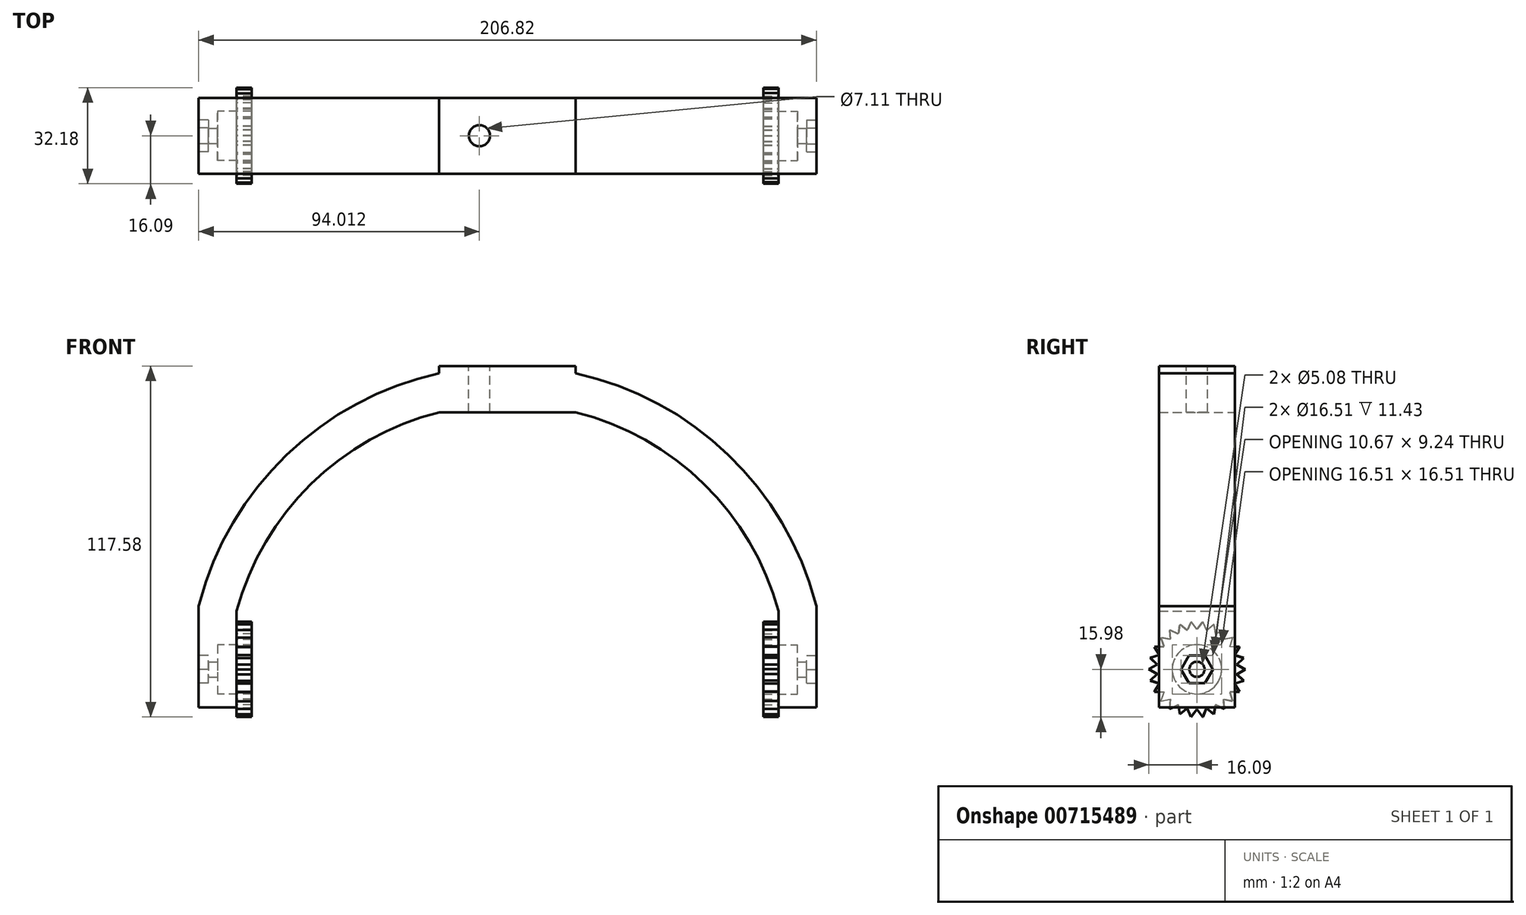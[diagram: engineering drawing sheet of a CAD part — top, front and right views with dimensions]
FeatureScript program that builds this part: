
annotation { "Feature Type Name" : "Feature", "Feature Type Description" : "" }
export const myFeature = defineFeature(function(context is Context, id is Id, definition is map)
    precondition{}
    {
        {
            var Q0;
            Q0=qCreatedBy(makeId("Front.planeOp"),FACE);
            var sketch = newSketch(context, id + "F0", { "sketchPlane" : qUnion([Q0])});
            skArc(sketch, "E0", {"start": v(97.06, 33.02) * mm, "mid": v(0, 107.95) * mm, "end": v(-97.06, 33.02) * mm});
            skLineSegment(sketch, "E1", {"start": v(-97.06, 33.02) * mm, "end": v(-97.06, 0) * mm});
            skLineSegment(sketch, "E2", {"start": v(97.06, 33.02) * mm, "end": v(97.06, 0) * mm});
            skSolve(sketch);
        }
        {
            var Q0;
            Q0=qCreatedBy(makeId("Top.planeOp"),FACE);
            var sketch = newSketch(context, id + "F1", { "sketchPlane" : qUnion([Q0])});
            skPoint(sketch, "E3.0", {"position": v(-97.06, 0) * mm});
            skLineSegment(sketch, "E4.bottom", {"start": v(-103.41, 12.7) * mm, "end": v(-90.71, 12.7) * mm});
            skLineSegment(sketch, "E4.top", {"start": v(-103.41, -12.7) * mm, "end": v(-90.71, -12.7) * mm});
            skLineSegment(sketch, "E4.left", {"start": v(-103.41, 12.7) * mm, "end": v(-103.41, -12.7) * mm});
            skLineSegment(sketch, "E4.right", {"start": v(-90.71, 12.7) * mm, "end": v(-90.71, -12.7) * mm});
            skSolve(sketch);
        }
        {
            var Q0;
            Q0=qSketchRegion(id+"F1",true);
            var Q1;
            Q1=qConstructionFilter(qBodyType(qCreatedBy(id+"F0",EDGE),BodyType.WIRE),ConstructionObject.NO);
            sweep(context, id + "F2", {"profiles" : qUnion([Q0]), "path" : qUnion([Q1])});
        }
        {
            var Q0;
            Q0=qCreatedBy(makeId("Right.planeOp"),FACE);
            var sketch = newSketch(context, id + "F3", { "sketchPlane" : qUnion([Q0])});
            skCircle(sketch, "E5", {"center": v(0, 12.7) * mm, "radius": 2.54 * mm});
            skSolve(sketch);
        }
        {
            var Q0;
            Q0=qSketchRegion(id+"F3",true);
            extrude(context, id + "F4", {"entities" : qUnion([Q0]), "operationType" : NewBodyOperationType.REMOVE, "endBound" : BoundingType.SYMMETRIC, "oppositeDirection" : true, "depth" : 254 * mm, "offsetDistance" : 25.4 * mm});
        }
        {
            var Q0;
            Q0=makeQuery(id+"F2.opSweep","SWEPT_FACE",FACE,{"disambiguationData":[OSD([sQuery(id+"F0.wireOp",EDGE,"E2"),sQuery(id+"F1.wireOp",EDGE,"E4.left")])]});
            var Q1;
            Q1=makeQuery(id+"F2.opSweep","CAP_VERTEX",VERTEX,{"disambiguationData":[OSD([sQuery(id+"F0.wireOp",EDGE,"E2"),sQuery(id+"F1.wireOp",EDGE,"E4.bottom"),sQuery(id+"F1.wireOp",EDGE,"E4.left")])],"isStart":false});
            cPlane(context, id + "F5", {"entities" : qUnion([Q0, Q1]), "cplaneType" : CPlaneType.PLANE_POINT, "offset" : 25.4 * mm, "width" : 152.4 * mm, "height" : 152.4 * mm});
        }
        {
            var Q0;
            Q0=qCreatedBy(id+"F5.planeOp",FACE);
            var sketch = newSketch(context, id + "F6", { "sketchPlane" : qUnion([Q0])});
            skCircle(sketch, "E6", {"center": v(0, 12.7) * mm, "radius": 5.33 * mm, "construction": true});
            skLineSegment(sketch, "E7.0", {"start": v(-2.67, 17.32) * mm, "end": v(2.67, 17.32) * mm});
            skLineSegment(sketch, "E7.1", {"start": v(2.67, 17.32) * mm, "end": v(5.33, 12.7) * mm});
            skLineSegment(sketch, "E7.2", {"start": v(5.33, 12.7) * mm, "end": v(2.67, 8.08) * mm});
            skLineSegment(sketch, "E7.3", {"start": v(2.67, 8.08) * mm, "end": v(-2.67, 8.08) * mm});
            skLineSegment(sketch, "E7.4", {"start": v(-2.67, 8.08) * mm, "end": v(-5.33, 12.7) * mm});
            skLineSegment(sketch, "E7.5", {"start": v(-5.33, 12.7) * mm, "end": v(-2.67, 17.32) * mm});
            skSolve(sketch);
        }
        {
            var Q0;
            Q0=makeQuery(id+"F6.imprint","IMPRINT",FACE,{"disambiguationData":[TD([[makeQuery(id+"F6.imprint","IMPRINT",EDGE,{"derivedFrom":sQuery(id+"F6.wireOp",EDGE,"E7.0")}),-1.0]])]});
            extrude(context, id + "F7", {"entities" : qUnion([Q0]), "operationType" : NewBodyOperationType.REMOVE, "oppositeDirection" : true, "depth" : 3.3 * mm, "offsetDistance" : 25.4 * mm});
        }
        {
            var Q0;
            Q0=makeQuery(id+"F2.opSweep","SWEPT_FACE",FACE,{"disambiguationData":[OSD([sQuery(id+"F0.wireOp",EDGE,"E1"),sQuery(id+"F1.wireOp",EDGE,"E4.left")])]});
            var Q1;
            Q1=makeQuery(id+"F2.opSweep","CAP_VERTEX",VERTEX,{"disambiguationData":[OSD([sQuery(id+"F0.wireOp",EDGE,"E1"),sQuery(id+"F1.wireOp",EDGE,"E4.bottom"),sQuery(id+"F1.wireOp",EDGE,"E4.left")])],"isStart":true});
            cPlane(context, id + "F8", {"entities" : qUnion([Q0, Q1]), "cplaneType" : CPlaneType.PLANE_POINT, "offset" : 25.4 * mm, "width" : 152.4 * mm, "height" : 152.4 * mm});
        }
        {
            var Q0;
            Q0=qCreatedBy(id+"F8.planeOp",FACE);
            var sketch = newSketch(context, id + "F9", { "sketchPlane" : qUnion([Q0])});
            skLineSegment(sketch, "E8", {"start": v(0, 0) * mm, "end": v(0, 12.7) * mm, "construction": true});
            skCircle(sketch, "E9", {"center": v(0, 12.7) * mm, "radius": 5.33 * mm, "construction": true});
            skLineSegment(sketch, "E10.0", {"start": v(-2.67, 17.32) * mm, "end": v(2.67, 17.32) * mm});
            skLineSegment(sketch, "E10.1", {"start": v(2.67, 17.32) * mm, "end": v(5.33, 12.7) * mm});
            skLineSegment(sketch, "E10.2", {"start": v(5.33, 12.7) * mm, "end": v(2.67, 8.08) * mm});
            skLineSegment(sketch, "E10.3", {"start": v(2.67, 8.08) * mm, "end": v(-2.67, 8.08) * mm});
            skLineSegment(sketch, "E10.4", {"start": v(-2.67, 8.08) * mm, "end": v(-5.33, 12.7) * mm});
            skLineSegment(sketch, "E10.5", {"start": v(-5.33, 12.7) * mm, "end": v(-2.67, 17.32) * mm});
            skSolve(sketch);
        }
        {
            var Q0;
            Q0=makeQuery(id+"F9.imprint","IMPRINT",FACE,{"disambiguationData":[TD([[makeQuery(id+"F9.imprint","IMPRINT",EDGE,{"derivedFrom":sQuery(id+"F9.wireOp",EDGE,"E10.0")}),-1.0]])]});
            extrude(context, id + "F10", {"entities" : qUnion([Q0]), "operationType" : NewBodyOperationType.REMOVE, "oppositeDirection" : true, "depth" : 3.3 * mm, "offsetDistance" : 25.4 * mm});
        }
        {
            var Q0;
            Q0=makeQuery(id+"F2.opSweep","SWEPT_FACE",FACE,{"disambiguationData":[OSD([sQuery(id+"F0.wireOp",EDGE,"E1"),sQuery(id+"F1.wireOp",EDGE,"E4.left")])]});
            cPlane(context, id + "F11", {"entities" : qUnion([Q0]), "cplaneType" : CPlaneType.OFFSET, "offset" : 6.35 * mm, "oppositeDirection" : true, "width" : 152.4 * mm, "height" : 152.4 * mm});
        }
        {
            var Q0;
            Q0=qCreatedBy(id+"F11.planeOp",FACE);
            var sketch = newSketch(context, id + "F12", { "sketchPlane" : qUnion([Q0])});
            skLineSegment(sketch, "E11", {"start": v(0, 0) * mm, "end": v(0, 12.7) * mm, "construction": true});
            skCircle(sketch, "E12", {"center": v(0, 12.7) * mm, "radius": 8.26 * mm});
            skSolve(sketch);
        }
        {
            var Q0;
            Q0=makeQuery(id+"F2.opSweep","SWEPT_FACE",FACE,{"disambiguationData":[OSD([sQuery(id+"F0.wireOp",EDGE,"E2"),sQuery(id+"F1.wireOp",EDGE,"E4.left")])]});
            cPlane(context, id + "F13", {"entities" : qUnion([Q0]), "cplaneType" : CPlaneType.OFFSET, "offset" : 6.35 * mm, "oppositeDirection" : true, "width" : 152.4 * mm, "height" : 152.4 * mm});
        }
        {
            var Q0;
            Q0=qCreatedBy(id+"F13.planeOp",FACE);
            var sketch = newSketch(context, id + "F14", { "sketchPlane" : qUnion([Q0])});
            skLineSegment(sketch, "E13", {"start": v(0, 0) * mm, "end": v(0, 12.7) * mm, "construction": true});
            skCircle(sketch, "E14", {"center": v(0, 12.7) * mm, "radius": 8.26 * mm});
            skSolve(sketch);
        }
        {
            var Q0;
            Q0=makeQuery(id+"F2.opSweep","SWEPT_FACE",FACE,{"disambiguationData":[OSD([sQuery(id+"F0.wireOp",EDGE,"E1"),sQuery(id+"F1.wireOp",EDGE,"E4.right")])]});
            var sketch = newSketch(context, id + "F15", { "sketchPlane" : qUnion([Q0])});
            skCircle(sketch, "E15", {"center": v(0, 12.7) * mm, "radius": 13.34 * mm, "construction": true});
            skLineSegment(sketch, "E16", {"start": v(-3.28, 25.63) * mm, "end": v(-2, 28.67) * mm});
            skLineSegment(sketch, "E17", {"start": v(-2, 28.67) * mm, "end": v(0, 26.04) * mm});
            skLineSegment(sketch, "E18.1.0", {"start": v(-6.27, 24.47) * mm, "end": v(-5.76, 27.73) * mm});
            skLineSegment(sketch, "E18.1.1", {"start": v(-5.76, 27.73) * mm, "end": v(-3.2, 25.65) * mm});
            skLineSegment(sketch, "E18.2.0", {"start": v(-8.9, 22.62) * mm, "end": v(-9.18, 25.91) * mm});
            skLineSegment(sketch, "E18.2.1", {"start": v(-9.18, 25.91) * mm, "end": v(-6.2, 24.5) * mm});
            skLineSegment(sketch, "E18.3.0", {"start": v(-11.02, 20.2) * mm, "end": v(-12.08, 23.33) * mm});
            skLineSegment(sketch, "E18.3.1", {"start": v(-12.08, 23.33) * mm, "end": v(-8.84, 22.68) * mm});
            skLineSegment(sketch, "E18.4.0", {"start": v(-12.5, 17.35) * mm, "end": v(-14.27, 20.13) * mm});
            skLineSegment(sketch, "E18.4.1", {"start": v(-14.27, 20.13) * mm, "end": v(-10.97, 20.28) * mm});
            skLineSegment(sketch, "E18.5.0", {"start": v(-13.25, 14.22) * mm, "end": v(-15.64, 16.5) * mm});
            skLineSegment(sketch, "E18.5.1", {"start": v(-15.64, 16.5) * mm, "end": v(-12.47, 17.43) * mm});
            skLineSegment(sketch, "E18.6.0", {"start": v(-13.23, 11) * mm, "end": v(-16.1, 12.65) * mm});
            skLineSegment(sketch, "E18.6.1", {"start": v(-16.1, 12.65) * mm, "end": v(-13.24, 14.3) * mm});
            skLineSegment(sketch, "E18.7.0", {"start": v(-12.44, 7.89) * mm, "end": v(-15.61, 8.8) * mm});
            skLineSegment(sketch, "E18.7.1", {"start": v(-15.61, 8.8) * mm, "end": v(-13.24, 11.1) * mm});
            skLineSegment(sketch, "E18.8.0", {"start": v(-10.92, 5.05) * mm, "end": v(-14.22, 5.17) * mm});
            skLineSegment(sketch, "E18.8.1", {"start": v(-14.22, 5.17) * mm, "end": v(-12.47, 7.97) * mm});
            skLineSegment(sketch, "E18.9.0", {"start": v(-8.78, 2.66) * mm, "end": v(-12, 1.99) * mm});
            skLineSegment(sketch, "E18.9.1", {"start": v(-12, 1.99) * mm, "end": v(-10.97, 5.12) * mm});
            skLineSegment(sketch, "E18.10.0", {"start": v(-6.12, 0.85) * mm, "end": v(-9.1, -0.57) * mm});
            skLineSegment(sketch, "E18.10.1", {"start": v(-9.1, -0.57) * mm, "end": v(-8.84, 2.72) * mm});
            skLineSegment(sketch, "E18.11.0", {"start": v(-3.1, -0.27) * mm, "end": v(-5.66, -2.37) * mm});
            skLineSegment(sketch, "E18.11.1", {"start": v(-5.66, -2.37) * mm, "end": v(-6.2, 0.9) * mm});
            skLineSegment(sketch, "E18.12.0", {"start": v(0.09, -0.63) * mm, "end": v(-1.89, -3.28) * mm});
            skLineSegment(sketch, "E18.12.1", {"start": v(-1.89, -3.28) * mm, "end": v(-3.2, -0.25) * mm});
            skLineSegment(sketch, "E18.13.0", {"start": v(3.28, -0.23) * mm, "end": v(2, -3.27) * mm});
            skLineSegment(sketch, "E18.13.1", {"start": v(2, -3.27) * mm, "end": v(0, -0.63) * mm});
            skLineSegment(sketch, "E18.14.0", {"start": v(6.27, 0.93) * mm, "end": v(5.76, -2.33) * mm});
            skLineSegment(sketch, "E18.14.1", {"start": v(5.76, -2.33) * mm, "end": v(3.2, -0.25) * mm});
            skLineSegment(sketch, "E18.15.0", {"start": v(8.9, 2.78) * mm, "end": v(9.18, -0.51) * mm});
            skLineSegment(sketch, "E18.15.1", {"start": v(9.18, -0.51) * mm, "end": v(6.2, 0.9) * mm});
            skLineSegment(sketch, "E18.16.0", {"start": v(11.02, 5.2) * mm, "end": v(12.08, 2.07) * mm});
            skLineSegment(sketch, "E18.16.1", {"start": v(12.08, 2.07) * mm, "end": v(8.84, 2.72) * mm});
            skLineSegment(sketch, "E18.17.0", {"start": v(12.5, 8.05) * mm, "end": v(14.27, 5.27) * mm});
            skLineSegment(sketch, "E18.17.1", {"start": v(14.27, 5.27) * mm, "end": v(10.97, 5.12) * mm});
            skLineSegment(sketch, "E18.18.0", {"start": v(13.25, 11.18) * mm, "end": v(15.64, 8.9) * mm});
            skLineSegment(sketch, "E18.18.1", {"start": v(15.64, 8.9) * mm, "end": v(12.47, 7.97) * mm});
            skLineSegment(sketch, "E18.19.0", {"start": v(13.23, 14.4) * mm, "end": v(16.1, 12.75) * mm});
            skLineSegment(sketch, "E18.19.1", {"start": v(16.1, 12.75) * mm, "end": v(13.24, 11.1) * mm});
            skLineSegment(sketch, "E18.20.0", {"start": v(12.44, 17.51) * mm, "end": v(15.61, 16.6) * mm});
            skLineSegment(sketch, "E18.20.1", {"start": v(15.61, 16.6) * mm, "end": v(13.24, 14.3) * mm});
            skLineSegment(sketch, "E18.21.0", {"start": v(10.92, 20.35) * mm, "end": v(14.22, 20.23) * mm});
            skLineSegment(sketch, "E18.21.1", {"start": v(14.22, 20.23) * mm, "end": v(12.47, 17.43) * mm});
            skLineSegment(sketch, "E18.22.0", {"start": v(8.78, 22.74) * mm, "end": v(12, 23.41) * mm});
            skLineSegment(sketch, "E18.22.1", {"start": v(12, 23.41) * mm, "end": v(10.97, 20.28) * mm});
            skLineSegment(sketch, "E18.23.0", {"start": v(6.12, 24.55) * mm, "end": v(9.1, 25.97) * mm});
            skLineSegment(sketch, "E18.23.1", {"start": v(9.1, 25.97) * mm, "end": v(8.84, 22.68) * mm});
            skLineSegment(sketch, "E18.24.0", {"start": v(3.1, 25.67) * mm, "end": v(5.66, 27.77) * mm});
            skLineSegment(sketch, "E18.24.1", {"start": v(5.66, 27.77) * mm, "end": v(6.2, 24.5) * mm});
            skLineSegment(sketch, "E18.25.0", {"start": v(-0.09, 26.03) * mm, "end": v(1.89, 28.68) * mm});
            skLineSegment(sketch, "E18.25.1", {"start": v(1.89, 28.68) * mm, "end": v(3.2, 25.65) * mm});
            skSolve(sketch);
        }
        {
            var Q0;
            Q0=qSketchRegion(id+"F15",true);
            extrude(context, id + "F16", {"entities" : qUnion([Q0]), "operationType" : NewBodyOperationType.ADD, "depth" : 5.08 * mm, "offsetDistance" : 25.4 * mm});
        }
        {
            var Q0;
            Q0=makeQuery(id+"F2.opSweep","SWEPT_FACE",FACE,{"disambiguationData":[OSD([sQuery(id+"F0.wireOp",EDGE,"E2"),sQuery(id+"F1.wireOp",EDGE,"E4.right")])]});
            var sketch = newSketch(context, id + "F17", { "sketchPlane" : qUnion([Q0])});
            skCircle(sketch, "E19", {"center": v(0, 12.7) * mm, "radius": 13.34 * mm, "construction": true});
            skLineSegment(sketch, "E20", {"start": v(-3.28, 25.63) * mm, "end": v(-2, 28.67) * mm});
            skLineSegment(sketch, "E21", {"start": v(-2, 28.67) * mm, "end": v(0, 26.04) * mm});
            skLineSegment(sketch, "E22.1.0", {"start": v(-5.76, 27.73) * mm, "end": v(-3.2, 25.65) * mm});
            skLineSegment(sketch, "E22.1.1", {"start": v(-6.27, 24.47) * mm, "end": v(-5.76, 27.73) * mm});
            skLineSegment(sketch, "E22.2.0", {"start": v(-9.18, 25.91) * mm, "end": v(-6.2, 24.5) * mm});
            skLineSegment(sketch, "E22.2.1", {"start": v(-8.9, 22.62) * mm, "end": v(-9.18, 25.91) * mm});
            skLineSegment(sketch, "E22.3.0", {"start": v(-12.08, 23.33) * mm, "end": v(-8.84, 22.68) * mm});
            skLineSegment(sketch, "E22.3.1", {"start": v(-11.02, 20.2) * mm, "end": v(-12.08, 23.33) * mm});
            skLineSegment(sketch, "E22.4.0", {"start": v(-14.27, 20.13) * mm, "end": v(-10.97, 20.28) * mm});
            skLineSegment(sketch, "E22.4.1", {"start": v(-12.5, 17.35) * mm, "end": v(-14.27, 20.13) * mm});
            skLineSegment(sketch, "E22.5.0", {"start": v(-15.64, 16.5) * mm, "end": v(-12.47, 17.43) * mm});
            skLineSegment(sketch, "E22.5.1", {"start": v(-13.25, 14.22) * mm, "end": v(-15.64, 16.5) * mm});
            skLineSegment(sketch, "E22.6.0", {"start": v(-16.1, 12.65) * mm, "end": v(-13.24, 14.3) * mm});
            skLineSegment(sketch, "E22.6.1", {"start": v(-13.23, 11) * mm, "end": v(-16.1, 12.65) * mm});
            skLineSegment(sketch, "E22.7.0", {"start": v(-15.61, 8.8) * mm, "end": v(-13.24, 11.1) * mm});
            skLineSegment(sketch, "E22.7.1", {"start": v(-12.44, 7.89) * mm, "end": v(-15.61, 8.8) * mm});
            skLineSegment(sketch, "E22.8.0", {"start": v(-14.22, 5.17) * mm, "end": v(-12.47, 7.97) * mm});
            skLineSegment(sketch, "E22.8.1", {"start": v(-10.92, 5.05) * mm, "end": v(-14.22, 5.17) * mm});
            skLineSegment(sketch, "E22.9.0", {"start": v(-12, 1.99) * mm, "end": v(-10.97, 5.12) * mm});
            skLineSegment(sketch, "E22.9.1", {"start": v(-8.78, 2.66) * mm, "end": v(-12, 1.99) * mm});
            skLineSegment(sketch, "E22.10.0", {"start": v(-9.1, -0.57) * mm, "end": v(-8.84, 2.72) * mm});
            skLineSegment(sketch, "E22.10.1", {"start": v(-6.12, 0.85) * mm, "end": v(-9.1, -0.57) * mm});
            skLineSegment(sketch, "E22.11.0", {"start": v(-5.66, -2.37) * mm, "end": v(-6.2, 0.9) * mm});
            skLineSegment(sketch, "E22.11.1", {"start": v(-3.1, -0.27) * mm, "end": v(-5.66, -2.37) * mm});
            skLineSegment(sketch, "E22.12.0", {"start": v(-1.89, -3.28) * mm, "end": v(-3.2, -0.25) * mm});
            skLineSegment(sketch, "E22.12.1", {"start": v(0.09, -0.63) * mm, "end": v(-1.89, -3.28) * mm});
            skLineSegment(sketch, "E22.13.0", {"start": v(2, -3.27) * mm, "end": v(0, -0.63) * mm});
            skLineSegment(sketch, "E22.13.1", {"start": v(3.28, -0.23) * mm, "end": v(2, -3.27) * mm});
            skLineSegment(sketch, "E22.14.0", {"start": v(5.76, -2.33) * mm, "end": v(3.2, -0.25) * mm});
            skLineSegment(sketch, "E22.14.1", {"start": v(6.27, 0.93) * mm, "end": v(5.76, -2.33) * mm});
            skLineSegment(sketch, "E22.15.0", {"start": v(9.18, -0.51) * mm, "end": v(6.2, 0.9) * mm});
            skLineSegment(sketch, "E22.15.1", {"start": v(8.9, 2.78) * mm, "end": v(9.18, -0.51) * mm});
            skLineSegment(sketch, "E22.16.0", {"start": v(12.08, 2.07) * mm, "end": v(8.84, 2.72) * mm});
            skLineSegment(sketch, "E22.16.1", {"start": v(11.02, 5.2) * mm, "end": v(12.08, 2.07) * mm});
            skLineSegment(sketch, "E22.17.0", {"start": v(14.27, 5.27) * mm, "end": v(10.97, 5.12) * mm});
            skLineSegment(sketch, "E22.17.1", {"start": v(12.5, 8.05) * mm, "end": v(14.27, 5.27) * mm});
            skLineSegment(sketch, "E22.18.0", {"start": v(15.64, 8.9) * mm, "end": v(12.47, 7.97) * mm});
            skLineSegment(sketch, "E22.18.1", {"start": v(13.25, 11.18) * mm, "end": v(15.64, 8.9) * mm});
            skLineSegment(sketch, "E22.19.0", {"start": v(16.1, 12.75) * mm, "end": v(13.24, 11.1) * mm});
            skLineSegment(sketch, "E22.19.1", {"start": v(13.23, 14.4) * mm, "end": v(16.1, 12.75) * mm});
            skLineSegment(sketch, "E22.20.0", {"start": v(15.61, 16.6) * mm, "end": v(13.24, 14.3) * mm});
            skLineSegment(sketch, "E22.20.1", {"start": v(12.44, 17.51) * mm, "end": v(15.61, 16.6) * mm});
            skLineSegment(sketch, "E22.21.0", {"start": v(14.22, 20.23) * mm, "end": v(12.47, 17.43) * mm});
            skLineSegment(sketch, "E22.21.1", {"start": v(10.92, 20.35) * mm, "end": v(14.22, 20.23) * mm});
            skLineSegment(sketch, "E22.22.0", {"start": v(12, 23.41) * mm, "end": v(10.97, 20.28) * mm});
            skLineSegment(sketch, "E22.22.1", {"start": v(8.78, 22.74) * mm, "end": v(12, 23.41) * mm});
            skLineSegment(sketch, "E22.23.0", {"start": v(9.1, 25.97) * mm, "end": v(8.84, 22.68) * mm});
            skLineSegment(sketch, "E22.23.1", {"start": v(6.12, 24.55) * mm, "end": v(9.1, 25.97) * mm});
            skLineSegment(sketch, "E22.24.0", {"start": v(5.66, 27.77) * mm, "end": v(6.2, 24.5) * mm});
            skLineSegment(sketch, "E22.24.1", {"start": v(3.1, 25.67) * mm, "end": v(5.66, 27.77) * mm});
            skLineSegment(sketch, "E22.25.0", {"start": v(1.89, 28.68) * mm, "end": v(3.2, 25.65) * mm});
            skLineSegment(sketch, "E22.25.1", {"start": v(-0.09, 26.03) * mm, "end": v(1.89, 28.68) * mm});
            skSolve(sketch);
        }
        {
            var Q0;
            Q0=qSketchRegion(id+"F17",true);
            var Q1;
            Q1=makeQuery(id+"F2.opSweep","SWEPT_FACE",FACE,{"disambiguationData":[OSD([sQuery(id+"F0.wireOp",EDGE,"E2"),sQuery(id+"F1.wireOp",EDGE,"E4.left")])]});
            extrude(context, id + "F18", {"entities" : qUnion([Q0, Q1]), "operationType" : NewBodyOperationType.ADD, "depth" : 5.08 * mm, "offsetDistance" : 25.4 * mm});
        }
        {
            var Q0;
            Q0=qSketchRegion(id+"F12",true);
            extrude(context, id + "F19", {"entities" : qUnion([Q0]), "operationType" : NewBodyOperationType.REMOVE, "oppositeDirection" : true, "depth" : 63.75 * mm, "offsetDistance" : 25.4 * mm});
        }
        {
            var Q0;
            Q0=qSketchRegion(id+"F14",true);
            extrude(context, id + "F20", {"entities" : qUnion([Q0]), "operationType" : NewBodyOperationType.REMOVE, "oppositeDirection" : true, "depth" : 25.4 * mm, "offsetDistance" : 25.4 * mm});
        }
        {
            var Q0;
            Q0=makeQuery(id+"F2.opSweep","SWEPT_EDGE",EDGE,{"disambiguationData":[OSD([sQuery(id+"F0.wireOp",EDGE,"E0"),sQuery(id+"F1.wireOp",EDGE,"E4.top"),sQuery(id+"F1.wireOp",EDGE,"E4.left")]),OD(2.0)]});
            cPoint(context, id + "F21", {"entities" : qUnion([Q0]), "parameter" : 0.5});
        }
        {
            var Q0;
            Q0=qCreatedBy(makeId("Top.planeOp"),FACE);
            var Q1;
            Q1=qCreatedBy(id+"F21",VERTEX);
            cPlane(context, id + "F22", {"entities" : qUnion([Q0, Q1]), "cplaneType" : CPlaneType.PLANE_POINT, "offset" : 25.4 * mm, "width" : 152.4 * mm, "height" : 152.4 * mm});
        }
        {
            var Q0;
            Q0=qCreatedBy(id+"F22.planeOp",FACE);
            var sketch = newSketch(context, id + "F23", { "sketchPlane" : qUnion([Q0])});
            skFitSpline(sketch, "E23.0", {"points": [v(-103.2, 12.7) * mm, v(-34.4, 12.7) * mm, v(34.4, 12.7) * mm, v(103.2, 12.7) * mm]});
            skLineSegment(sketch, "E24.bottom", {"start": v(-22.86, 12.7) * mm, "end": v(22.86, 12.7) * mm});
            skLineSegment(sketch, "E24.top", {"start": v(-22.86, -12.7) * mm, "end": v(22.86, -12.7) * mm});
            skLineSegment(sketch, "E24.left", {"start": v(-22.86, 12.7) * mm, "end": v(-22.86, -12.7) * mm});
            skLineSegment(sketch, "E24.right", {"start": v(22.86, 12.7) * mm, "end": v(22.86, -12.7) * mm});
            skPoint(sketch, "E24.middle", {"position": v(0, 0) * mm});
            skSolve(sketch);
        }
        {
            var Q0;
            Q0=qSketchRegion(id+"F23",true);
            extrude(context, id + "F24", {"entities" : qUnion([Q0]), "operationType" : NewBodyOperationType.ADD, "oppositeDirection" : true, "depth" : 15.5 * mm, "offsetDistance" : 25.4 * mm});
        }
        {
            var Q0;
            Q0=qCreatedBy(id+"F22.planeOp",FACE);
            var sketch = newSketch(context, id + "F25", { "sketchPlane" : qUnion([Q0])});
            skCircle(sketch, "E25", {"center": v(-9.4, 0) * mm, "radius": 3.56 * mm});
            skCircle(sketch, "E26.MirrorC", {"center": v(9.4, 0) * mm, "radius": 3.56 * mm});
            skSolve(sketch);
        }
        {
            var Q0;
            Q0=makeQuery(id+"F25.imprint","IMPRINT",FACE,{"disambiguationData":[TD([[makeQuery(id+"F25.imprint","IMPRINT",EDGE,{"derivedFrom":sQuery(id+"F25.wireOp",EDGE,"E25")}),1.0]])]});
            var Q1;
            Q1=makeQuery(id+"F25.imprint","IMPRINT",FACE,{"disambiguationData":[TD([[makeQuery(id+"F25.imprint","IMPRINT",EDGE,{"derivedFrom":sQuery(id+"F25.wireOp",EDGE,"E26.MirrorC")}),-1.0]])]});
            extrude(context, id + "F26", {"entities" : qUnion([Q0, Q1]), "operationType" : NewBodyOperationType.REMOVE, "oppositeDirection" : true, "depth" : 25.4 * mm, "offsetDistance" : 25.4 * mm});
        }
    });
